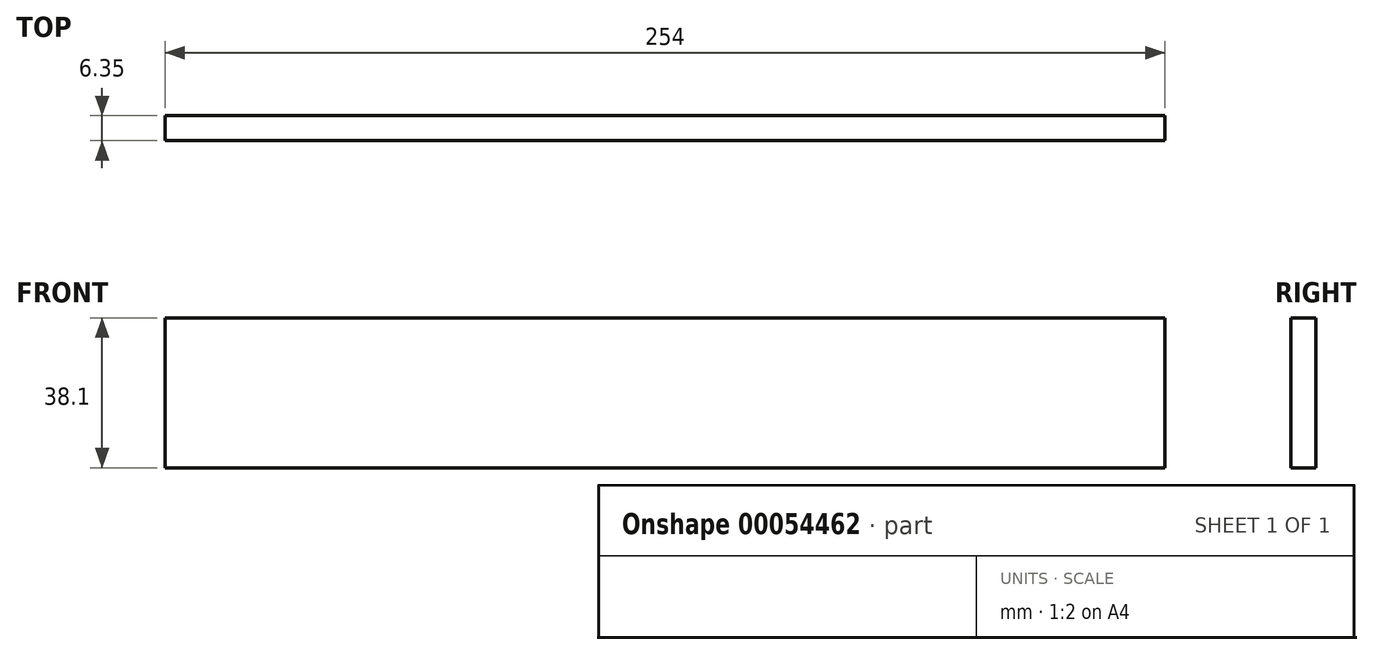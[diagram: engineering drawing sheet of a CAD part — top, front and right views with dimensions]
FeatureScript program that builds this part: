
annotation { "Feature Type Name" : "Feature", "Feature Type Description" : "" }
export const myFeature = defineFeature(function(context is Context, id is Id, definition is map)
    precondition{}
    {
        {
            var Q0;
            Q0=qCreatedBy(makeId("Front.planeOp"),FACE);
            var sketch = newSketch(context, id + "F0", { "sketchPlane" : qUnion([Q0])});
            skLineSegment(sketch, "E0.rect.bottom", {"start": v(127, 19.05) * mm, "end": v(-127, 19.05) * mm});
            skLineSegment(sketch, "E0.rect.top", {"start": v(127, -19.05) * mm, "end": v(-127, -19.05) * mm});
            skLineSegment(sketch, "E0.rect.left", {"start": v(127, 19.05) * mm, "end": v(127, -19.05) * mm});
            skLineSegment(sketch, "E0.rect.right", {"start": v(-127, 19.05) * mm, "end": v(-127, -19.05) * mm});
            skPoint(sketch, "E0.rect.middle", {"position": v(0, 0) * mm});
            skSolve(sketch);
        }
        {
            var Q0;
            Q0 = qSketchRegion(id + "F0", true);
            extrude(context, id + "F1", {"entities" : qUnion([Q0]), "oppositeDirection" : true, "depth" : 6.35 * mm});
        }
    });
